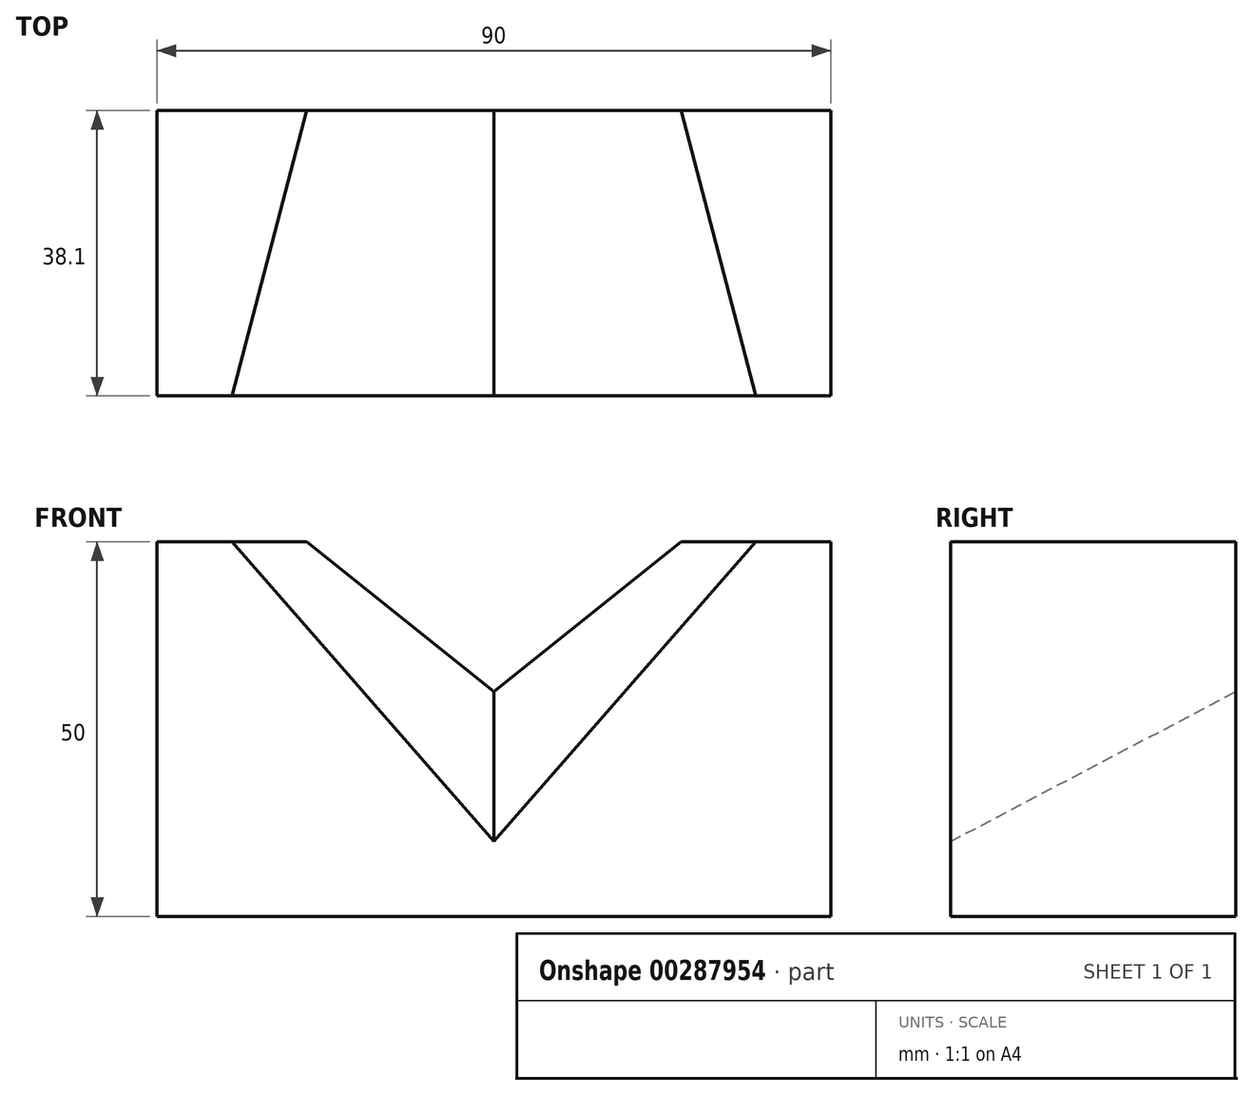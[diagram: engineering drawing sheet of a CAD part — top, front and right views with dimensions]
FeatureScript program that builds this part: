
annotation { "Feature Type Name" : "Feature", "Feature Type Description" : "" }
export const myFeature = defineFeature(function(context is Context, id is Id, definition is map)
    precondition{}
    {
        {
            var Q0;
            Q0=qCreatedBy(makeId("Front.planeOp"),FACE);
            var sketch = newSketch(context, id + "F0", { "sketchPlane" : qUnion([Q0])});
            skLineSegment(sketch, "E0.bottom", {"start": v(-55.3, 22.64) * mm, "end": v(34.7, 22.64) * mm});
            skLineSegment(sketch, "E0.top", {"start": v(-55.3, 72.64) * mm, "end": v(34.7, 72.64) * mm});
            skLineSegment(sketch, "E0.left", {"start": v(-55.3, 22.64) * mm, "end": v(-55.3, 72.64) * mm});
            skLineSegment(sketch, "E0.right", {"start": v(34.7, 22.64) * mm, "end": v(34.7, 72.64) * mm});
            skSolve(sketch);
        }
        {
            var Q0;
            Q0=makeQuery(id+"F0.imprint","IMPRINT",FACE,{"disambiguationData":[TD([[makeQuery(id+"F0.imprint","IMPRINT",EDGE,{"derivedFrom":sQuery(id+"F0.wireOp",EDGE,"E0.bottom")}),1.0]])]});
            extrude(context, id + "F1", {"entities" : qUnion([Q0]), "depth" : 38.1 * mm});
        }
        {
            var Q0;
            Q0=makeQuery(id+"F1.opExtrude","CAP_FACE",FACE,{"disambiguationData":[OSD([sQuery(id+"F0.wireOp",EDGE,"E0.bottom"),sQuery(id+"F0.wireOp",EDGE,"E0.top"),sQuery(id+"F0.wireOp",EDGE,"E0.left"),sQuery(id+"F0.wireOp",EDGE,"E0.right")])],"isStart":false});
            var sketch = newSketch(context, id + "F2", { "sketchPlane" : qUnion([Q0])});
            skLineSegment(sketch, "E1", {"start": v(-45.3, 72.64) * mm, "end": v(-10.3, 32.64) * mm});
            skLineSegment(sketch, "E2", {"start": v(-10.3, 32.64) * mm, "end": v(24.7, 72.64) * mm});
            skSolve(sketch);
        }
        {
            var Q0;
            Q0=makeQuery(id+"F1.opExtrude","CAP_FACE",FACE,{"disambiguationData":[OSD([sQuery(id+"F0.wireOp",EDGE,"E0.bottom"),sQuery(id+"F0.wireOp",EDGE,"E0.top"),sQuery(id+"F0.wireOp",EDGE,"E0.left"),sQuery(id+"F0.wireOp",EDGE,"E0.right")])],"isStart":true});
            var sketch = newSketch(context, id + "F3", { "sketchPlane" : qUnion([Q0])});
            skLineSegment(sketch, "E3", {"start": v(-14.7, 72.64) * mm, "end": v(10.3, 52.64) * mm});
            skLineSegment(sketch, "E4", {"start": v(10.3, 52.64) * mm, "end": v(35.3, 72.64) * mm});
            skSolve(sketch);
        }
        {
            var Q1;
            {var subQ0=sQuery(id+"F2.wireOp",EDGE,"E1");Q1=makeQuery(id+"F2.imprint","IMPRINT",FACE,{"disambiguationData":[TD([[makeQuery(id+"F2.imprint","IMPRINT",EDGE,{"derivedFrom":subQ0}),1.0]])]});}
            var Q2;
            {var subQ0=sQuery(id+"F3.wireOp",EDGE,"E3");Q2=makeQuery(id+"F3.imprint","IMPRINT",FACE,{"disambiguationData":[TD([[makeQuery(id+"F3.imprint","IMPRINT",EDGE,{"derivedFrom":subQ0}),1.0]])]});}
            loft(context, id + "F4", {"operationType" : NewBodyOperationType.REMOVE, "sheetProfilesArray" : [{ "sheetProfileEntities" : qUnion([Q1]) }, { "sheetProfileEntities" : qUnion([Q2]) }]});
        }
    });
